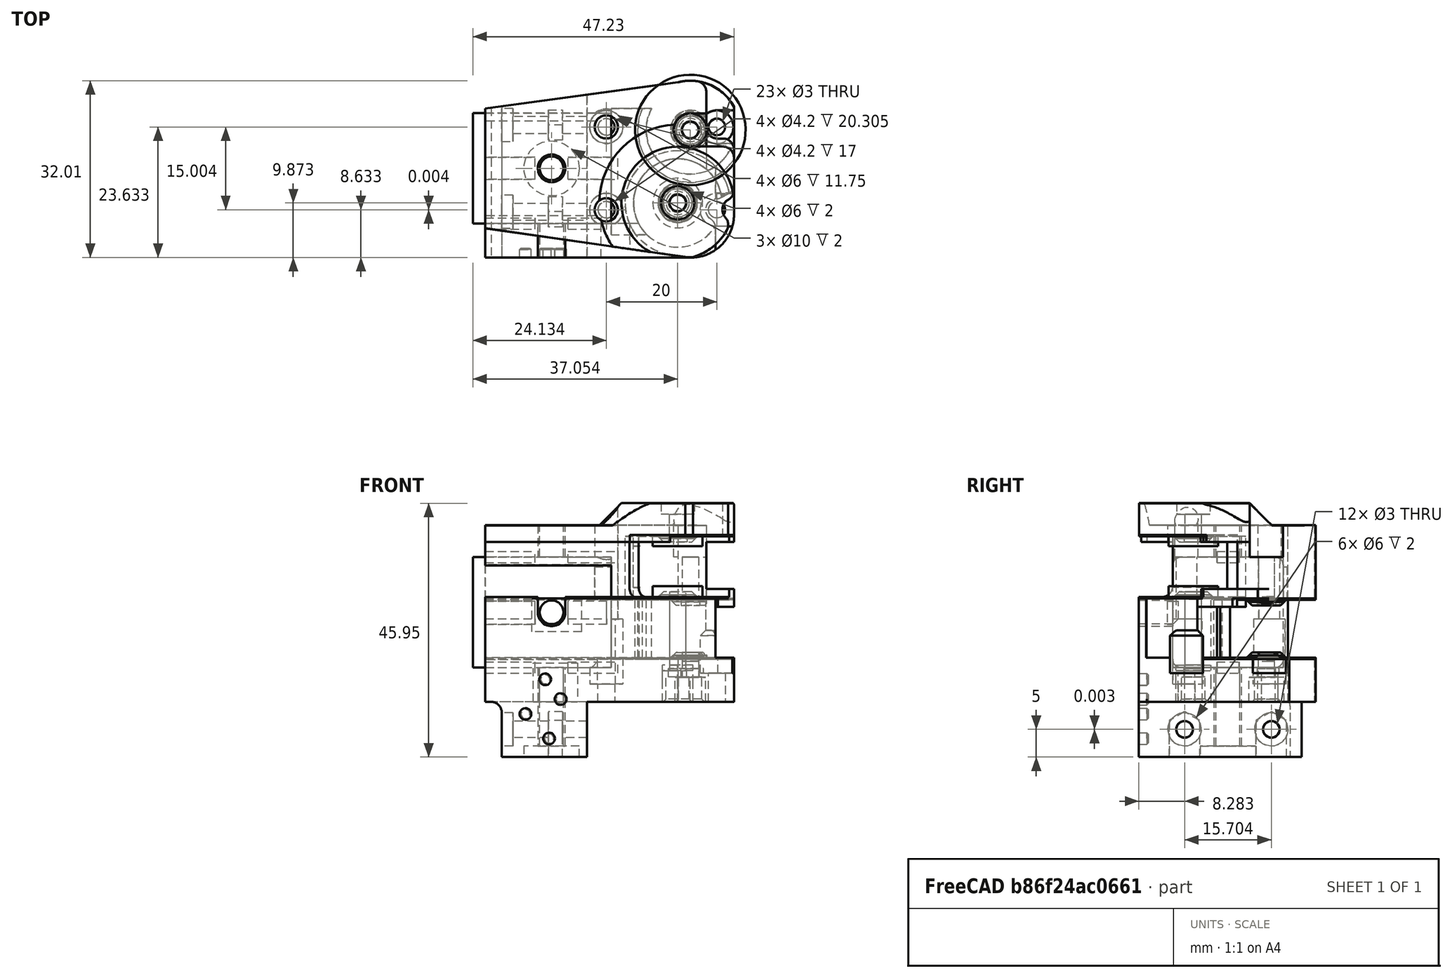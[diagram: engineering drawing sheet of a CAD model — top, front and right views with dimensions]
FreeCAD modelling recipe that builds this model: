
FCSTD DOCUMENT  (FreeCAD 0.18R16146 (Git))
Label: carrier-CF-right
License: All rights reserved
LicenseURL: http://en.wikipedia.org/wiki/All_rights_reserved
objects: Part::Cylinder×17, Part::Cut×12, Part::Box×11, Part::MultiFuse×8, Part::Chamfer×7, Part::Feature×7, Mesh::Feature×1
note: 62 computed .brp shape members not serialized (recipe doc carries the construction recipe); baked Part::Feature solids carry a one-line shape summary decoded from their .brp

FEATURE [Part::Box] Box003  label="Cube003"
  AttacherType = Attacher::AttachEngine3D
  Height = 2
  Length = 9
  Placement = pos=(-20.93,14.39,15.2) rot=(0,0,1;0rad)
  Width = 4
FEATURE [Part::Box] Box004  label="Cube004"
  AttacherType = Attacher::AttachEngine3D
  Height = 2
  Length = 9
  Placement = pos=(-5.93,14.39,15.2) rot=(0,0,1;0rad)
  Width = 4
FEATURE [Part::Box] Box005  label="Cube005"
  AttacherType = Attacher::AttachEngine3D
  Height = 2
  Length = 9
  Placement = pos=(-5.93,14.39,35.2) rot=(0,0,1;0rad)
  Width = 4
FEATURE [Part::Box] Box006  label="Cube006"
  AttacherType = Attacher::AttachEngine3D
  Height = 2
  Length = 9
  Placement = pos=(-20.93,14.39,35.2) rot=(0,0,1;0rad)
  Width = 4
FEATURE [Part::Box] Box007  label="Cube007"
  AttacherType = Attacher::AttachEngine3D
  Height = 4.2
  Length = 9
  Placement = pos=(-20.93,5.39,24) rot=(0,0,1;0rad)
  Width = 2
FEATURE [Part::Box] Box008  label="Cube008"
  AttacherType = Attacher::AttachEngine3D
  Height = 4.2
  Length = 7
  Placement = pos=(-5.93,5.39,24) rot=(0,0,1;0rad)
  Width = 2
FEATURE [Part::Chamfer] Chamfer
  Base = -> Box008
  Edges = 1 edges r=1: [Edge11]
FEATURE [Part::Chamfer] Chamfer001
  Base = -> Box007
  Edges = 1 edges r=1: [Edge11]
FEATURE [Part::MultiFuse] Fusion
  Shapes = -> [Chamfer001,Chamfer,Box006,Box005,Box004,Box003]
FEATURE [Part::Feature] Part__Feature199  label="Y_Carriage_RIGHT_Body (1)"
  Placement = pos=(-664.031,179.424,-461.938) rot=(1,0,0;1.5708rad)
  shape: bbox 48.82 x 34.51 x 45.95 mm, 173 faces (baked)
FEATURE [Part::Cylinder] Cylinder  label="ois-1"
  Angle = 360
  AttacherType = Attacher::AttachEngine3D
  Height = 2
  Placement = pos=(13.89,10.12,28.95) rot=(0,0,1;0rad)
  Radius = 4.5
FEATURE [Part::Cylinder] Cylinder009
  Angle = 360
  AttacherType = Attacher::AttachEngine3D
  Height = 0.75
  Placement = pos=(13.89,10.12,28.7) rot=(0,0,1;0rad)
  Radius = 1.5
FEATURE [Part::Cylinder] Cylinder010
  Angle = 360
  AttacherType = Attacher::AttachEngine3D
  Height = 0.75
  Placement = pos=(13.89,10.12,28.7) rot=(0,0,1;0rad)
  Radius = 3.5
FEATURE [Part::Cylinder] Cylinder011
  Angle = 360
  AttacherType = Attacher::AttachEngine3D
  Height = 0.75
  Placement = pos=(16.18,23.33,17.7) rot=(0,0,1;0rad)
  Radius = 3
FEATURE [Part::Cylinder] Cylinder012
  Angle = 360
  AttacherType = Attacher::AttachEngine3D
  Height = 11
  Placement = pos=(16.18,23.33,17.7) rot=(0,0,1;0rad)
  Radius = 10
FEATURE [Part::Cylinder] Cylinder013
  Angle = 360
  AttacherType = Attacher::AttachEngine3D
  Height = 0.75
  Placement = pos=(16.18,23.33,17.7) rot=(0,0,1;0rad)
  Radius = 1.5
FEATURE [Mesh::Feature] carrier_right  label="carrier-right"
FEATURE [Part::Feature] Part__Feature113  label="Y_CarriageHT_RIGHT_Body (1)"
  Placement = pos=(-664.031,179.424,-461.938) rot=(1,0,0;1.5708rad)
  shape: bbox 48.82 x 34.51 x 45.95 mm, 188 faces (baked)
FEATURE [Part::Box] Box010  label="Cube010"
  AttacherType = Attacher::AttachEngine3D
  Height = 20
  Length = 25
  Placement = pos=(-23.16,6.39,16.2) rot=(0,0,1;0rad)
  Width = 20
FEATURE [Part::Cylinder] Cylinder015
  Angle = 360
  AttacherType = Attacher::AttachEngine3D
  Height = 2
  Placement = pos=(13.89,10.12,38.2) rot=(0,0,1;0rad)
  Radius = 4.5
FEATURE [Part::Cylinder] Cylinder016
  Angle = 360
  AttacherType = Attacher::AttachEngine3D
  Height = 2
  Placement = pos=(13.89,10.12,28.7) rot=(0,0,1;0rad)
  Radius = 8
FEATURE [Part::Cylinder] Cylinder017
  Angle = 360
  AttacherType = Attacher::AttachEngine3D
  Height = 2
  Placement = pos=(13.89,10.12,38.2) rot=(0,0,1;0rad)
  Radius = 8
FEATURE [Part::Cut] Cut006003004
  Base = -> Cylinder010
  Tool = -> Cylinder009
FEATURE [Part::Feature] Cut006003004001  label="Cut006003005"
  Placement = pos=(0,0,10.75) rot=(0,0,1;0rad)
  shape: bbox 7 x 7 x 0.75 mm, 4 faces (baked)
FEATURE [Part::Chamfer] Chamfer002
  Base = -> Cut006003004001
  Edges = 1 edges r=0.5: [Edge3]
  Placement = pos=(0,0,0.1) rot=(0,0,1;0rad)
FEATURE [Part::Chamfer] Chamfer003
  Base = -> Cut006003004
  Edges = 1 edges r=0.5: [Edge1]
  Placement = pos=(0,0,-0.1) rot=(0,0,1;0rad)
FEATURE [Part::Cylinder] Cylinder014
  Angle = 360
  AttacherType = Attacher::AttachEngine3D
  Height = 5
  Placement = pos=(20.97,23.88,17) rot=(0,0,1;1.5708rad)
  Radius = 3
FEATURE [Part::Cut] Cut006003004003
  Base = -> Cylinder011
  Tool = -> Cylinder013
FEATURE [Part::Feature] Cut006003004003001  label="Cut006003004004"
  Placement = pos=(0,0,10.6) rot=(0,0,1;0rad)
  shape: bbox 6 x 6 x 0.75 mm, 4 faces (baked)
FEATURE [Part::Feature] Cut006003004003002  label="Cut006003004005"
  Placement = pos=(0,0,-0.35) rot=(0,0,1;0rad)
  shape: bbox 6 x 6 x 0.75 mm, 4 faces (baked)
FEATURE [Part::Chamfer] Chamfer004
  Base = -> Cut006003004003002
  Edges = 1 edges r=0.5: [Edge1]
FEATURE [Part::Cut] Cut006003004003003
  Base = -> Chamfer004
  Tool = -> Cylinder014
FEATURE [Part::Chamfer] Chamfer005
  Base = -> Cut006003004003001
  Edges = 1 edges r=0.5: [Edge3]
FEATURE [Part::Box] Box  label="Cube"
  AttacherType = Attacher::AttachEngine3D
  Height = 10
  Length = 10
  Placement = pos=(19.07,19.6,23.8) rot=(0,0,1;0rad)
  Width = 10
FEATURE [Part::Cut] Cut006003004003004
  Base = -> Chamfer005
  Tool = -> Box
FEATURE [Part::MultiFuse] Fusion001
  Shapes = -> [Cut006003004003004,Cut006003004003003,Chamfer002,Chamfer003]
FEATURE [Part::Feature] Fusion003001_solid  label="rev-1-exp"
  shape: bbox 48.82 x 34.51 x 45.95 mm, 242 faces (baked)
FEATURE [Part::Cut] Cut
  Base = -> Fusion003001_solid
  Tool = -> Cylinder016
FEATURE [Part::Cut] Cut006003004003005
  Base = -> Cut
  Tool = -> Cylinder017
FEATURE [Part::Cut] Cut006003004003006
  Base = -> Cut006003004003005
  Tool = -> Cylinder012
FEATURE [Part::MultiFuse] Fusion002  label="std-r1"
  Shapes = -> [Cut006003004003006,Fusion001]
FEATURE [Part::Cylinder] Cylinder018
  Angle = 360
  AttacherType = Attacher::AttachEngine3D
  Height = 4.5
  Placement = pos=(13.89,10.12,10) rot=(0,0,1;0rad)
  Radius = 2.1
FEATURE [Part::Cylinder] Cylinder020
  Angle = 360
  AttacherType = Attacher::AttachEngine3D
  Height = 4.5
  Placement = pos=(16.18,23.33,10) rot=(0,0,1;0rad)
  Radius = 2.1
FEATURE [Part::Cylinder] Cylinder021
  Angle = 360
  AttacherType = Attacher::AttachEngine3D
  Height = 5
  Placement = pos=(20.97,23.88,15.2) rot=(0,0,1;1.5708rad)
  Radius = 3
FEATURE [Part::Cylinder] Cylinder022
  Angle = 360
  AttacherType = Attacher::AttachEngine3D
  Height = 6
  Placement = pos=(13.89,10.12,10) rot=(0,0,1;0rad)
  Radius = 1.65
FEATURE [Part::Cylinder] Cylinder023
  Angle = 360
  AttacherType = Attacher::AttachEngine3D
  Height = 6
  Placement = pos=(16.18,23.33,10) rot=(0,0,1;0rad)
  Radius = 1.65
FEATURE [Part::Feature] Fusion002_solid  label="Fusion002 (Solid)"
  shape: bbox 48.82 x 34.51 x 45.95 mm, 267 faces (baked)
FEATURE [Part::Cylinder] Cylinder024
  Angle = 360
  AttacherType = Attacher::AttachEngine3D
  Height = 6
  Placement = pos=(16.18,23.33,10) rot=(0,0,1;0rad)
  Radius = 3.3
FEATURE [Part::Cylinder] Cylinder025
  Angle = 360
  AttacherType = Attacher::AttachEngine3D
  Height = 6
  Placement = pos=(13.89,10.12,10) rot=(0,0,1;0rad)
  Radius = 3.3
FEATURE [Part::MultiFuse] Fusion006
  Shapes = -> [Cylinder025,Cylinder024]
FEATURE [Part::MultiFuse] Fusion007
  Shapes = -> [Fusion006,Fusion002_solid]
FEATURE [Part::MultiFuse] Fusion008
  Shapes = -> [Cylinder018,Cylinder020]
FEATURE [Part::Cut] Cut006003004003007
  Base = -> Fusion007
  Tool = -> Fusion008
FEATURE [Part::MultiFuse] Fusion009
  Shapes = -> [Cylinder022,Cylinder023]
FEATURE [Part::Cut] Cut006003004003008
  Base = -> Cut006003004003007
  Tool = -> Fusion009
FEATURE [Part::Cut] Cut006003004003009
  Base = -> Cut006003004003008
  Tool = -> Cylinder021
FEATURE [Part::Chamfer] Chamfer006
  Base = -> Cut006003004003009
  Edges = 2 edges r=0.5: [Edge720,Edge721]
FEATURE [Part::Box] Box011  label="Cube011"
  AttacherType = Attacher::AttachEngine3D
  Height = 13
  Length = 22
  Placement = pos=(-24,-6,-3) rot=(0,0,1;0rad)
  Width = 38
FEATURE [Part::Cut] Cut006003004003010
  Base = -> Chamfer006
  Tool = -> Box011
FEATURE [Part::Box] Box012  label="Cube012"
  AttacherType = Attacher::AttachEngine3D
  Height = 7
  Length = 8
  Placement = pos=(-12.25,0.25,10) rot=(0,0,1;0rad)
  Width = 2
FEATURE [Part::MultiFuse] Fusion010
  Shapes = -> [Box012,Cut006003004003010]
FEATURE [Part::Box] Box013  label="Cube013"
  AttacherType = Attacher::AttachEngine3D
  Height = 20
  Length = 28
  Placement = pos=(-26.16,6.39,16.2) rot=(0,0,1;0rad)
  Width = 20
FEATURE [Part::Cut] Cut006003004003011
  Base = -> Fusion010
  Tool = -> Box013
